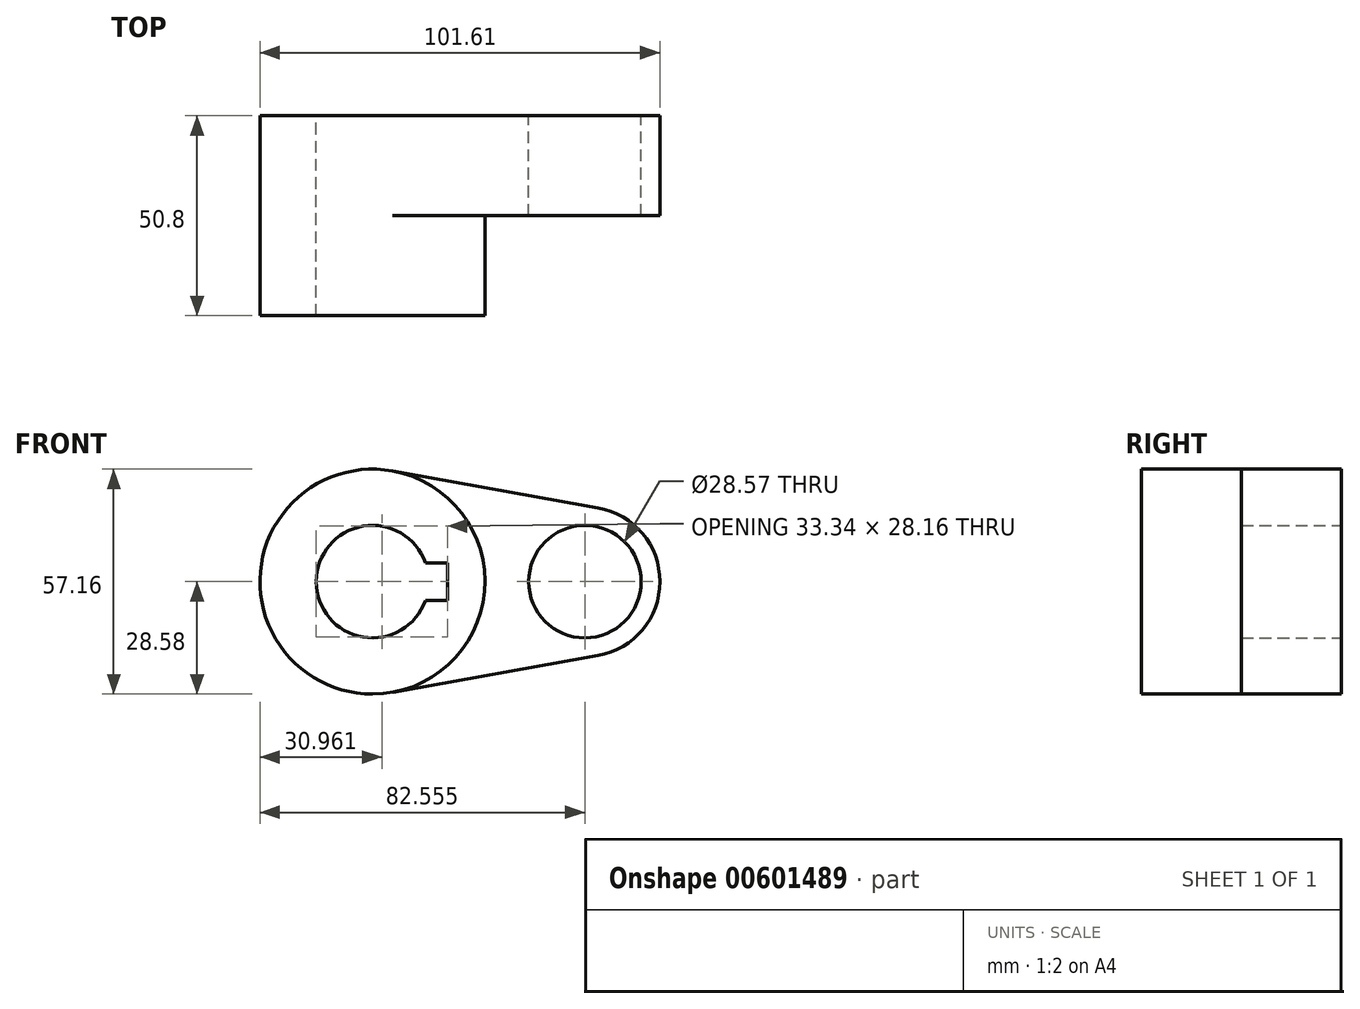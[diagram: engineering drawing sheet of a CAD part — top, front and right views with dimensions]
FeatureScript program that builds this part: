
annotation { "Feature Type Name" : "Feature", "Feature Type Description" : "" }
export const myFeature = defineFeature(function(context is Context, id is Id, definition is map)
    precondition{}
    {
        {
            var Q0;
            Q0=qCreatedBy(makeId("Front.planeOp"),FACE);
            var sketch = newSketch(context, id + "F0", { "sketchPlane" : qUnion([Q0])});
            skCircle(sketch, "E0", {"center": v(0, 0) * mm, "radius": 28.58 * mm});
            skCircle(sketch, "E1", {"center": v(53.98, 0) * mm, "radius": 19.05 * mm});
            skLineSegment(sketch, "E2", {"start": v(5.04, 28.13) * mm, "end": v(57.34, 18.75) * mm});
            skLineSegment(sketch, "E3", {"start": v(5.04, -28.13) * mm, "end": v(57.34, -18.75) * mm});
            skCircle(sketch, "E4", {"center": v(0, 0) * mm, "radius": 14.29 * mm});
            skCircle(sketch, "E5", {"center": v(53.98, 0) * mm, "radius": 14.29 * mm});
            skLineSegment(sketch, "E6.bottom", {"start": v(-19.05, 4.76) * mm, "end": v(19.05, 4.76) * mm});
            skLineSegment(sketch, "E6.top", {"start": v(-19.05, -4.76) * mm, "end": v(19.05, -4.76) * mm});
            skLineSegment(sketch, "E6.left", {"start": v(-19.05, 4.76) * mm, "end": v(-19.05, -4.76) * mm});
            skLineSegment(sketch, "E6.right", {"start": v(19.05, 4.76) * mm, "end": v(19.05, -4.76) * mm});
            skSolve(sketch);
        }
        {
            var Q0;
            {var subQ7=sQuery(id+"F0.wireOp",EDGE,"E6.left");Q0=makeQuery(id+"F0.imprint","IMPRINT",FACE,{"disambiguationData":[TD([[makeQuery(id+"F0.imprint","IMPRINT",EDGE,{"derivedFrom":subQ7}),-1.0]])]});}
            var Q1;
            {var subQ0=sQuery(id+"F0.wireOp",EDGE,"E2");Q1=makeQuery(id+"F0.imprint","IMPRINT",FACE,{"disambiguationData":[TD([[makeQuery(id+"F0.imprint","IMPRINT",EDGE,{"derivedFrom":subQ0}),-1.0]])]});}
            var Q2;
            {var subQ5=sQuery(id+"F0.wireOp",EDGE,"E6.left");Q2=makeQuery(id+"F0.imprint","IMPRINT",FACE,{"disambiguationData":[TD([[makeQuery(id+"F0.imprint","IMPRINT",EDGE,{"derivedFrom":subQ5}),1.0]])]});}
            var Q3;
            Q3=makeQuery(id+"F0.imprint","IMPRINT",FACE,{"disambiguationData":[TD([[makeQuery(id+"F0.imprint","IMPRINT",EDGE,{"derivedFrom":sQuery(id+"F0.wireOp",EDGE,"E5")}),-1.0]])]});
            extrude(context, id + "F1", {"entities" : qUnion([Q0, Q1, Q2, Q3]), "depth" : 25.4 * mm, "offsetDistance" : 25.4 * mm});
        }
        {
            var Q0;
            {var subQ7=sQuery(id+"F0.wireOp",EDGE,"E6.left");Q0=makeQuery(id+"F0.imprint","IMPRINT",FACE,{"disambiguationData":[TD([[makeQuery(id+"F0.imprint","IMPRINT",EDGE,{"derivedFrom":subQ7}),-1.0]])]});}
            var Q1;
            {var subQ5=sQuery(id+"F0.wireOp",EDGE,"E6.left");Q1=makeQuery(id+"F0.imprint","IMPRINT",FACE,{"disambiguationData":[TD([[makeQuery(id+"F0.imprint","IMPRINT",EDGE,{"derivedFrom":subQ5}),1.0]])]});}
            extrude(context, id + "F2", {"entities" : qUnion([Q0, Q1]), "operationType" : NewBodyOperationType.ADD, "depth" : 50.8 * mm, "offsetDistance" : 25.4 * mm});
        }
    });
